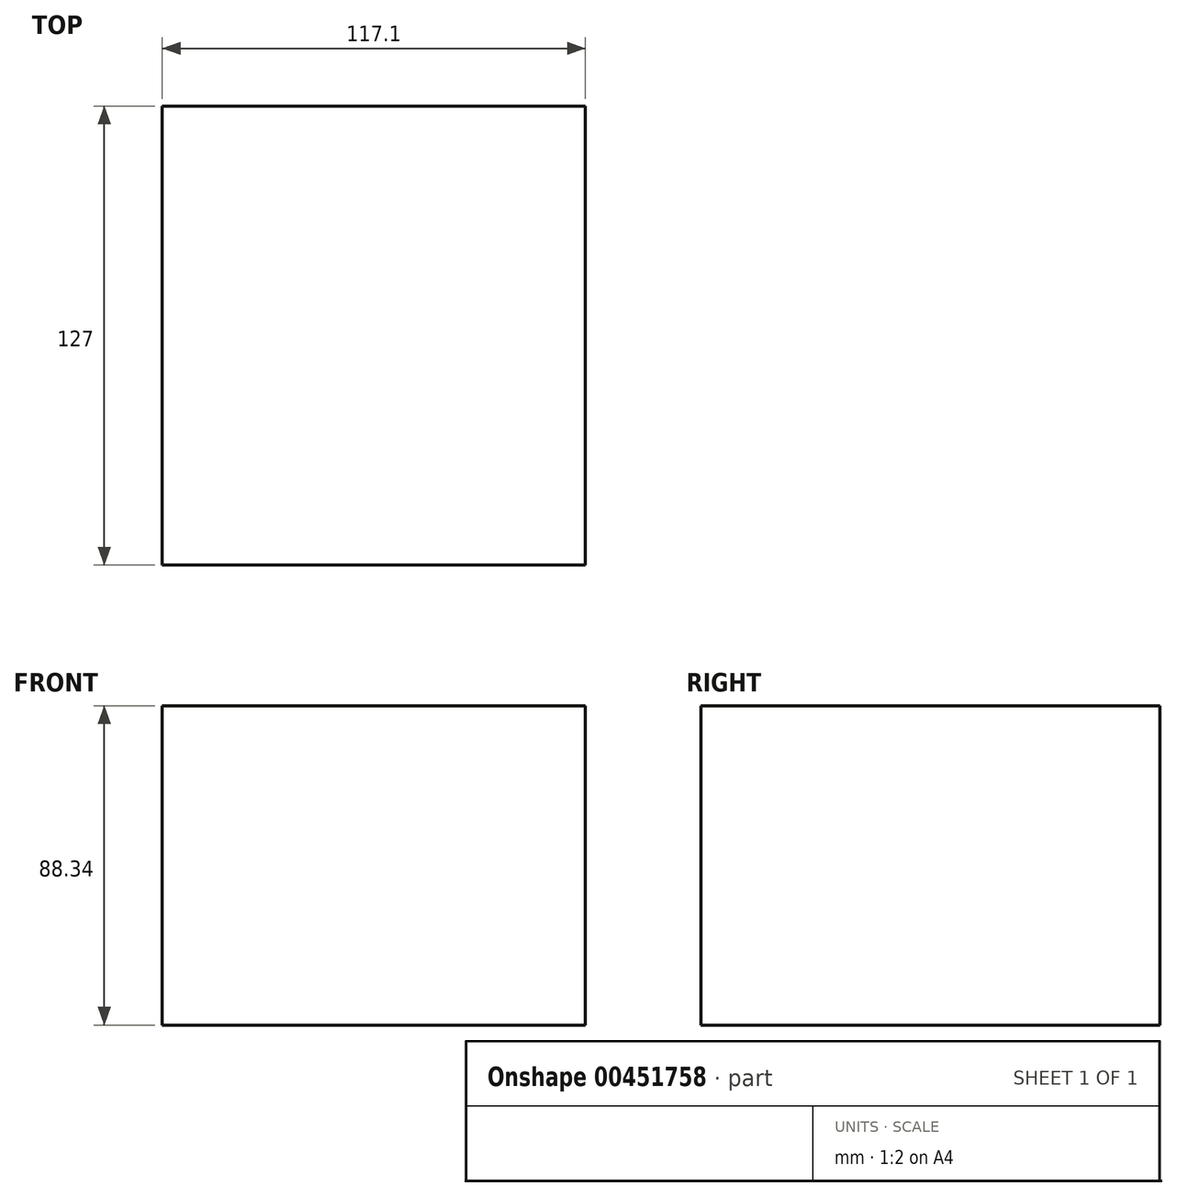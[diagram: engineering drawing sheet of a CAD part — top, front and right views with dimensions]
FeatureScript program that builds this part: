
annotation { "Feature Type Name" : "Feature", "Feature Type Description" : "" }
export const myFeature = defineFeature(function(context is Context, id is Id, definition is map)
    precondition{}
    {
        {
            var Q0;
            Q0=qCreatedBy(makeId("Front.planeOp"),FACE);
            var sketch = newSketch(context, id + "F0", { "sketchPlane" : qUnion([Q0])});
            skLineSegment(sketch, "E0.bottom", {"start": v(-69.44, 47.45) * mm, "end": v(47.66, 47.45) * mm});
            skLineSegment(sketch, "E0.top", {"start": v(-69.44, -40.89) * mm, "end": v(47.66, -40.89) * mm});
            skLineSegment(sketch, "E0.left", {"start": v(-69.44, 47.45) * mm, "end": v(-69.44, -40.89) * mm});
            skLineSegment(sketch, "E1", {"start": v(47.66, 47.45) * mm, "end": v(47.66, -40.89) * mm});
            skPoint(sketch, "E2", {"position": v(0, 22.1) * mm});
            skSolve(sketch);
        }
        {
            var Q0;
            Q0 = qSketchRegion(id + "F0", true);
            extrude(context, id + "F1", {"entities" : qUnion([Q0]), "depth" : 127 * mm});
        }
    });
